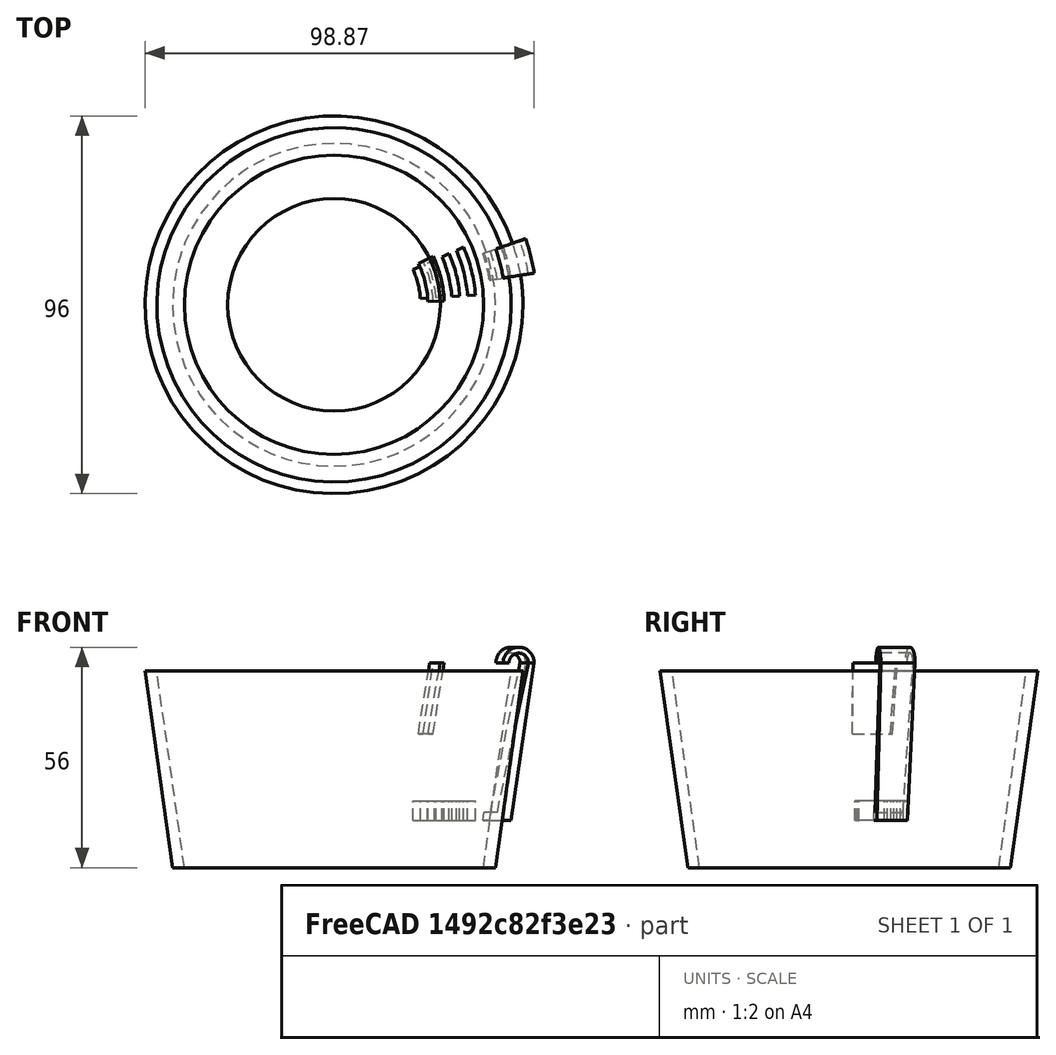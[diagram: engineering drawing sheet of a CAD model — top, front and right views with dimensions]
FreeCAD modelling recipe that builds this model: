
FCSTD DOCUMENT  (FreeCAD 0.14R3702 (Git))
Label: toothbrush-head-holder
License: CC-BY 3.0
LicenseURL: http://creativecommons.org/licenses/by/3.0/
objects: Part::Cone×9, Part::Cut×7, Sketcher::SketchObject×3, Mesh::Feature×2, Part::Sweep×1, PartDesign::Pocket×1
note: 22 computed .brp shape members not serialized (recipe doc carries the construction recipe); baked Part::Feature solids carry a one-line shape summary decoded from their .brp

FEATURE [Part::Cone] Cone  label="Indvendig"
  Angle = 360
  Height = 50
  Radius1 = 38
  Radius2 = 45
FEATURE [Part::Cone] Cone001  label="Udvendig"
  Angle = 360
  Height = 50
  Radius1 = 41
  Radius2 = 48
FEATURE [Part::Cut] Cut  label="Krus"
  Base = -> Cone001
  Tool = -> Cone
FEATURE [Part::Cone] Cone002  label="Ydre væg solid"
  Angle = 28
  Height = 40
  Placement = pos=(0,0,12) rot=(0,0,1;0rad)
  Radius1 = 38
  Radius2 = 45
FEATURE [Part::Cone] Cone003  label="Ydre væg og bund cutter"
  Angle = 24
  Height = 39
  Placement = pos=(0,0,13) rot=(0,0,1;0.034907rad)
  Radius1 = 36.5
  Radius2 = 43.5
FEATURE [Part::Cut] Cut001  label="Ydre væg og bund"
  Base = -> Cone002
  Tool = -> Cone003
FEATURE [Part::Cone] Cone004  label="Indre væg solid"
  Angle = 26
  Height = 18
  Placement = pos=(0,0,34) rot=(0,0,1;0rad)
  Radius1 = 25.2
  Radius2 = 28
FEATURE [Part::Cone] Cone006  label="Indre total cutter"
  Angle = 28
  Height = 40
  Placement = pos=(0,0,12) rot=(0,0,1;0rad)
  Radius1 = 20
  Radius2 = 27
FEATURE [Part::Cut] Cut003  label="Ydre væg og sider"
  Base = -> Cut001
  Tool = -> Cone006
FEATURE [Part::Cut] Cut004  label="Indre væg"
  Base = -> Cone004
  Tool = -> Cone006
FEATURE [Part::Cut] Cut005  label="Afgrænset inderside"
  Base = -> Cut004
  Tool = -> Cut003
FEATURE [Part::Cone] Cone007  label="Ydra hank cutter"
  Angle = 30
  Height = 38
  Placement = pos=(0,0,14) rot=(0,0,1;0rad)
  Radius1 = 42
  Radius2 = 50
FEATURE [Part::Cone] Cone008  label="Ydra hank solid"
  Angle = 10
  Height = 40
  Placement = pos=(0,0,12) rot=(0,0,1;0.15708rad)
  Radius1 = 45.5
  Radius2 = 51.5
FEATURE [Part::Cut] Cut006  label="Hank lodret"
  Base = -> Cone008
  Tool = -> Cone007
FEATURE [Sketcher::SketchObject] Sketch  label="Ydre hank path sketch"
  Placement = pos=(0,0,52) rot=(0,0,1;0rad)
  Support = -> Cut006 [Face2]
  sketch-geometry (1):
    g0: ArcOfCircle CenterX=0 CenterY=0 CenterZ=0 NormalX=0 NormalY=0 NormalZ=1 Radius=51.5 StartAngle=0.157099 EndAngle=0.331604
  constraints (1):
    c: Coincident(g0,g-1)
FEATURE [Sketcher::SketchObject] Sketch010  label="Hank sketch"
  Placement = pos=(0,0,0) rot=(0.993863,0.078219,0.078219;1.57695rad)
  Support = -> Cut006 [Face5]
  sketch-geometry (4):
    g0: ArcOfCircle CenterX=47.5 CenterY=52 CenterZ=0 NormalX=0 NormalY=0 NormalZ=1 Radius=2.5 StartAngle=0 EndAngle=3.14159
    g1: ArcOfCircle CenterX=47.5 CenterY=52 CenterZ=0 NormalX=0 NormalY=0 NormalZ=1 Radius=4 StartAngle=0 EndAngle=3.14159
    g2: LineSegment StartX=43.5 StartY=52 StartZ=0 EndX=45 EndY=52 EndZ=0
    g3: LineSegment StartX=50 StartY=52 StartZ=0 EndX=51.5 EndY=52 EndZ=0
  constraints (9):
    c: Coincident(g1,g0)
    c: Coincident(g2,g1)
    c: PointOnObject(g2,g0)
    c: Horizontal(g2)
    c: Coincident(g3,g0)
    c: PointOnObject(g3,g1)
    c: Horizontal(g3)
    c: Coincident(g0,g2)
    c: Coincident(g1,g3)
FEATURE [Part::Sweep] Sweep  label="Hank overbue"
  Frenet = false
  Sections = -> [Sketch010]
  Solid = true
  Spine = -> Sketch [Edge1]
  Transition = 1
FEATURE [Sketcher::SketchObject] Sketch011  label="Bundhuller sketch"
  Placement = pos=(0,0,12) rot=(1,0,0;3.14159rad)
  Support = -> Cut003 [Face4]
  sketch-geometry (16):
    g0: ArcOfCircle CenterX=0 CenterY=0 CenterZ=0 NormalX=0 NormalY=0 NormalZ=1 Radius=22 StartAngle=5.86489 EndAngle=6.21369
    g1: ArcOfCircle CenterX=0 CenterY=0 CenterZ=0 NormalX=0 NormalY=0 NormalZ=1 Radius=24 StartAngle=5.86489 EndAngle=6.21369
    g2: ArcOfCircle CenterX=0 CenterY=0 CenterZ=0 NormalX=0 NormalY=0 NormalZ=1 Radius=26 StartAngle=5.86489 EndAngle=6.21369
    g3: ArcOfCircle CenterX=0 CenterY=0 CenterZ=0 NormalX=0 NormalY=0 NormalZ=1 Radius=28.0002 StartAngle=5.86489 EndAngle=6.21369
    g4: ArcOfCircle CenterX=0 CenterY=0 CenterZ=0 NormalX=0 NormalY=0 NormalZ=1 Radius=30 StartAngle=5.86489 EndAngle=6.21369
    g5: ArcOfCircle CenterX=0 CenterY=0 CenterZ=0 NormalX=0 NormalY=0 NormalZ=1 Radius=32 StartAngle=5.86489 EndAngle=6.21369
    g6: ArcOfCircle CenterX=0 CenterY=0 CenterZ=0 NormalX=0 NormalY=0 NormalZ=1 Radius=34.0002 StartAngle=5.86489 EndAngle=6.21369
    g7: ArcOfCircle CenterX=0 CenterY=0 CenterZ=0 NormalX=0 NormalY=0 NormalZ=1 Radius=36.0002 StartAngle=5.86489 EndAngle=6.21369
    g8: LineSegment StartX=21.9469 StartY=-1.52777 StartZ=0 EndX=23.9421 EndY=-1.66666 EndZ=0
    g9: LineSegment StartX=20.1032 StartY=-8.93648 StartZ=0 EndX=21.9308 EndY=-9.74889 EndZ=0
    g10: LineSegment StartX=25.9372 StartY=-1.80555 StartZ=0 EndX=27.9326 EndY=-1.94445 EndZ=0
    g11: LineSegment StartX=29.9276 StartY=-2.08332 StartZ=0 EndX=31.9227 EndY=-2.22221 EndZ=0
    g12: LineSegment StartX=33.9181 StartY=-2.36111 StartZ=0 EndX=35.9133 EndY=-2.5 EndZ=0
    g13: LineSegment StartX=23.7583 StartY=-10.5613 StartZ=0 EndX=25.5861 EndY=-11.3738 EndZ=0
    g14: LineSegment StartX=27.4135 StartY=-12.1861 StartZ=0 EndX=29.241 EndY=-12.9985 EndZ=0
    g15: LineSegment StartX=31.0688 StartY=-13.811 StartZ=0 EndX=32.8964 EndY=-14.6234 EndZ=0
  constraints (28):
    c: Coincident(g0,g-1)
    c: Coincident(g2,g-1)
    c: Coincident(g3,g-1)
    c: Coincident(g4,g-1)
    c: Coincident(g6,g-1)
    c: Coincident(g7,g-1)
    c: Tangent(g8,g10)
    c: Tangent(g10,g11)
    c: Tangent(g11,g12)
    c: Tangent(g9,g13)
    c: Tangent(g13,g14)
    c: Tangent(g14,g15)
    c: Coincident(g7,g15)
    c: Coincident(g6,g15)
    c: Coincident(g5,g14)
    c: Coincident(g4,g14)
    c: Coincident(g3,g13)
    c: Coincident(g2,g13)
    c: Coincident(g1,g9)
    c: Coincident(g9,g0)
    c: Coincident(g0,g8)
    c: Coincident(g1,g8)
    c: Coincident(g2,g10)
    c: Coincident(g3,g10)
    c: Coincident(g4,g11)
    c: Coincident(g5,g11)
    c: Coincident(g6,g12)
    c: Coincident(g7,g12)
FEATURE [PartDesign::Pocket] Pocket  label="Bundhullet bund"
  Length = 5
  Sketch = -> Sketch011
  Type = 0
FEATURE [Part::Cone] Cone009  label="Ydra hank cutter nedre"
  Angle = 30
  Height = 40
  Placement = pos=(0,0,12) rot=(0,0,1;0rad)
  Radius1 = 40
  Radius2 = 47
FEATURE [Part::Cut] Cut007  label="Total cuttet hank"
  Base = -> Cut006
  Tool = -> Cone009
FEATURE [Mesh::Feature] test
FEATURE [Mesh::Feature] test001
  Placement = pos=(0,0,0) rot=(0,0,1;0.453786rad)
